# Revit family: NV Lounge
name_source: partatom
category: Furniture
units: mm (PartAtom-declared; Revit-internal decimal feet)

## family parameters
Always vertical = Yes
Cut with Voids When Loaded = No
OmniClass Number = 23.40.20.00
OmniClass Title = General Furniture and Specialties
Room Calculation Point = No
Shared = No
Work Plane-Based = No

## types (18) — shared parameters
Manufacturer = AIS Inc
Product = NV LOUNGE
URL = https://www.ais-inc.com
zero-valued in all types: Default Elevation

## per-type parameters (varying)
| type | Description | LNV1 | LNV1C | LNV1TL | LNV1TLC | LNV1TR | LNV1TRC | LNV2 | LNV2C | LNV2TL | LNV2TLC | LNV2TR | LNV2TRC | LNV3 | LNV3C | LNV3TL | LNV3TLC | LNV3TR | LNV3TRC |
| LNV1 | 34Wx33Dx34H NV Club Chair, Metal Legs | Yes | No | No | No | No | No | No | No | No | No | No | No | No | No | No | No | No | No |
| LNV1TR | 34Wx33Dx34H NV Club Chair, Metal Legs. Tablet RH | No | No | No | No | Yes | No | No | No | No | No | No | No | No | No | No | No | No | No |
| LNV1TL | 34Wx33Dx34H NV Club Chair, Metal Legs. Tablet LH | No | No | Yes | No | No | No | No | No | No | No | No | No | No | No | No | No | No | No |
| LNV2 | 54Wx34Dx33H NV 2-Seater, Metal Legs | No | No | No | No | No | No | Yes | No | No | No | No | No | No | No | No | No | No | No |
| LNV2TL | 54Wx34Dx33H NV 2-Seater, Metal Legs, Tablet LH | No | No | No | No | No | No | No | No | Yes | No | No | No | No | No | No | No | No | No |
| LNV2TR | 54Wx34Dx33H NV 2-Seater, Metal Legs, Tablet RH | No | No | No | No | No | No | No | No | No | No | Yes | No | No | No | No | No | No | No |
| LNV3 | 79Wx33Dx34H NV 3-Seater, Metal Legs | No | No | No | No | No | No | No | No | No | No | No | No | Yes | No | No | No | No | No |
| LNV3TL | 79Wx33Dx34H NV 3-Seater, Metal Legs, Tablet LH | No | No | No | No | No | No | No | No | No | No | No | No | No | No | Yes | No | No | No |
| LNV3TR | 79Wx33Dx34H NV 3-Seater, Metal Legs, Tablet RH | No | No | No | No | No | No | No | No | No | No | No | No | No | No | No | No | Yes | No |
| LNV1C | 34Wx33Dx34H NV Club Chair, Metal Legs, Configurable | No | Yes | No | No | No | No | No | No | No | No | No | No | No | No | No | No | No | No |
| LNV1TLC | 34Wx33Dx34H NV Club Chair, metal legs, tablet LH, configurable | No | No | No | Yes | No | No | No | No | No | No | No | No | No | No | No | No | No | No |
| LNV1TRC | 34Wx33Dx34H NV Club Chair, metal legs, tablet RH, configurable | No | No | No | No | No | Yes | No | No | No | No | No | No | No | No | No | No | No | No |
| LNV2C | 54Wx34Dx33H NV 2-Seater, metal legs, Configurable | No | No | No | No | No | No | No | Yes | No | No | No | No | No | No | No | No | No | No |
| LNV2TLC | 54Wx34Dx33H NV 2-Seater, metal legs, tablet LH, Configurable | No | No | No | No | No | No | No | No | No | Yes | No | No | No | No | No | No | No | No |
| LNV2TRC | 54Wx34Dx33H NV 2-Seater, metal legs, tablet RH, Configurable | No | No | No | No | No | No | No | No | No | No | No | Yes | No | No | No | No | No | No |
| LNV3C | 79Wx33Dx34H NV 3-Seater, metal legs, Configurable | No | No | No | No | No | No | No | No | No | No | No | No | No | Yes | No | No | No | No |
| LNV3TLC | 79Wx33Dx34H NV 3-Seater, metal legs, tablet LH, Configurable | No | No | No | No | No | No | No | No | No | No | No | No | No | No | No | Yes | No | No |
| LNV3TRC | 79Wx33Dx34H NV 3-Seater, metal legs, tablet RH, Configurable | No | No | No | No | No | No | No | No | No | No | No | No | No | No | No | No | No | Yes |

note: column(s) folded — value = type name in every type: Model

## geometry (parser evidence)
native form markers: Sweep x3
no freeform markers — native parametric forms only
